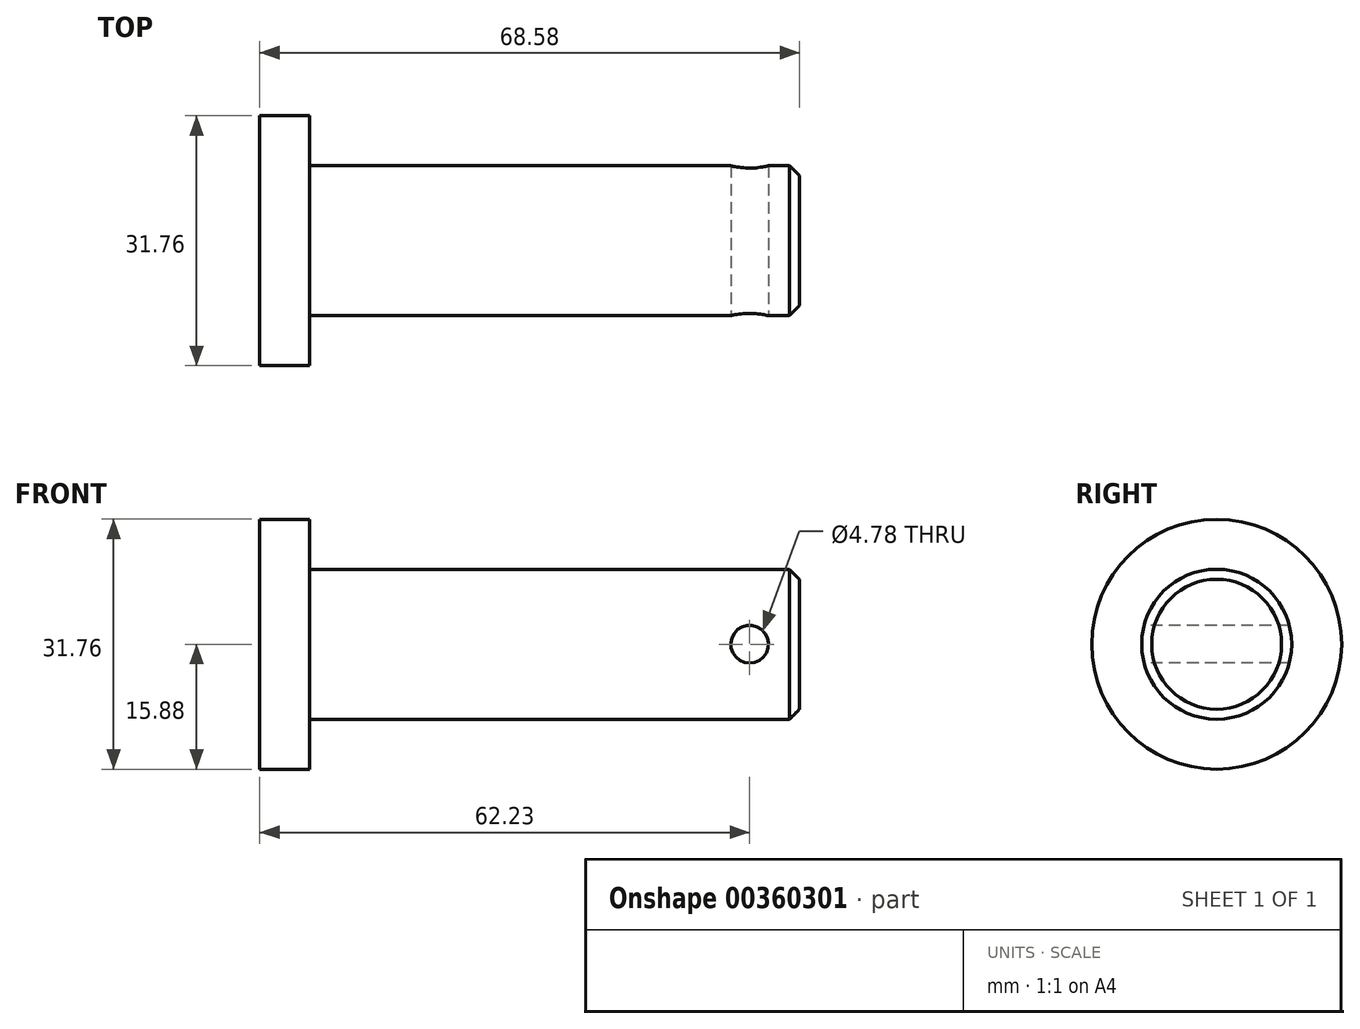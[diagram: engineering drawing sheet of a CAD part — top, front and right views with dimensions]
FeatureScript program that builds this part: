
annotation { "Feature Type Name" : "Feature", "Feature Type Description" : "" }
export const myFeature = defineFeature(function(context is Context, id is Id, definition is map)
    precondition{}
    {
        {
            var Q0;
            Q0=qCreatedBy(makeId("Right.planeOp"),FACE);
            var sketch = newSketch(context, id + "F0", { "sketchPlane" : qUnion([Q0])});
            skCircle(sketch, "E0", {"center": v(0, 0) * mm, "radius": 15.88 * mm});
            skSolve(sketch);
        }
        {
            var Q0;
            Q0 = qSketchRegion(id + "F0", true);
            extrude(context, id + "F1", {"entities" : qUnion([Q0]), "depth" : 6.35 * mm});
        }
        {
            var Q0;
            Q0=makeQuery(id+"F1.opExtrude","CAP_FACE",FACE,{"disambiguationData":[OSD([sQuery(id+"F0.wireOp",EDGE,"E0")])],"isStart":false});
            var sketch = newSketch(context, id + "F2", { "sketchPlane" : qUnion([Q0])});
            skCircle(sketch, "E1", {"center": v(0, 0) * mm, "radius": 9.53 * mm});
            skSolve(sketch);
        }
        {
            var Q0;
            Q0 = qSketchRegion(id + "F2", true);
            extrude(context, id + "F3", {"entities" : qUnion([Q0]), "operationType" : NewBodyOperationType.ADD, "depth" : 62.23 * mm});
        }
        {
            var Q0;
            Q0=makeQuery(id+"F3.opExtrude","CAP_EDGE",EDGE,{"disambiguationData":[OSD([sQuery(id+"F2.wireOp",EDGE,"E1")])],"isStart":false});
            chamfer(context, id + "F4", {"entities" : qUnion([Q0]), "chamferType" : ChamferType.OFFSET_ANGLE, "width" : 1.27 * mm, "oppositeDirection" : false, "angle" : 45 * degree, "tangentPropagation" : true});
        }
        {
            var Q0;
            Q0=qCreatedBy(makeId("Front.planeOp"),FACE);
            var sketch = newSketch(context, id + "F5", { "sketchPlane" : qUnion([Q0])});
            skLineSegment(sketch, "E2", {"start": v(0, 0) * mm, "end": v(62.23, 0) * mm, "construction": true});
            skCircle(sketch, "E3", {"center": v(62.23, 0) * mm, "radius": 2.39 * mm});
            skSolve(sketch);
        }
        {
            var Q0;
            Q0 = qSketchRegion(id + "F5", true);
            extrude(context, id + "F6", {"entities" : qUnion([Q0]), "operationType" : NewBodyOperationType.REMOVE, "endBound" : BoundingType.THROUGH_ALL, "oppositeDirection" : true, "depth" : 25.4 * mm, "hasSecondDirection" : true, "secondDirectionOppositeDirection" : false, "secondDirectionDepth" : 25.4 * mm});
        }
    });
